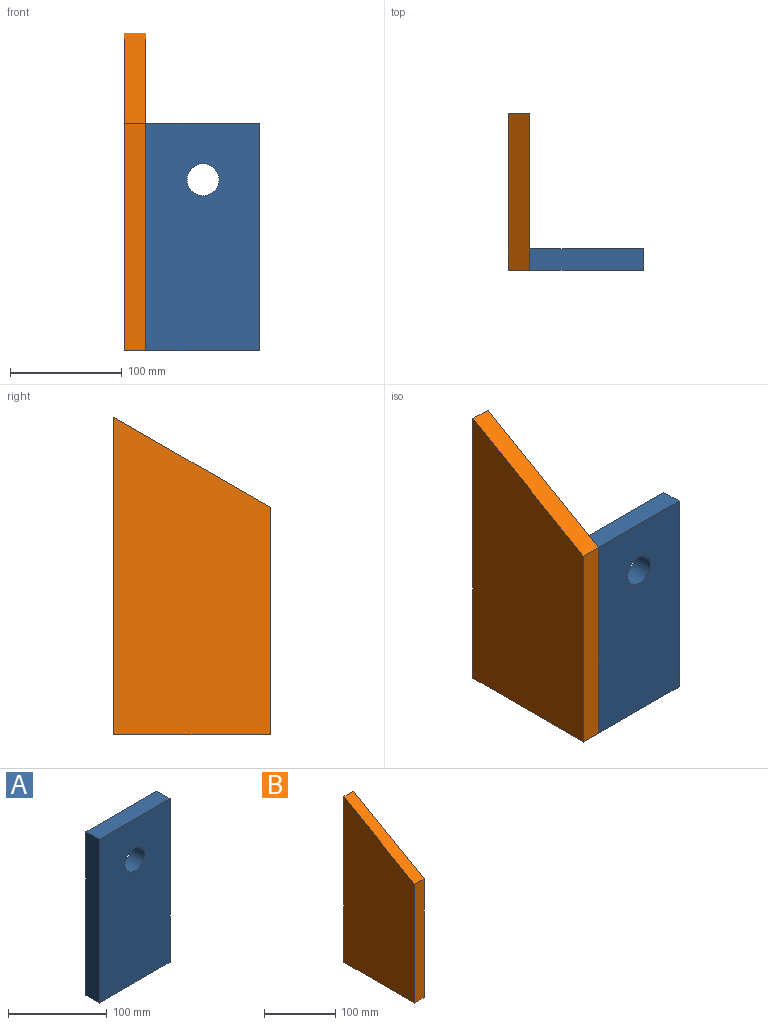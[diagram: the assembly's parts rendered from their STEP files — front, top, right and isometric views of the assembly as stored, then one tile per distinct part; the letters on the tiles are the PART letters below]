
ASSEMBLY  parts=2 mates=1
PART A: 7 faces, bbox 101.6x19.1x203.2 mm
  f0: plane 203.2x19.05mm, normal (-1,0,0), area 3871mm2, adj f1,f3,f5,f6
  f1: plane 101.6x19.05mm, normal (0,0,-1), area 1935.5mm2, adj f0,f2,f5,f6
  f2: plane 203.2x19.05mm, normal (1,0,0), area 3871mm2, adj f1,f3,f5,f6
  f3: plane 101.6x19.05mm, normal (0,0,1), area 1935.5mm2, adj f0,f2,f5,f6
  f4: cylinder r=14.29mm len=28.58mm, axis (0,1,0), area 1710.1mm2, adj f5,f6
  f5: plane 203.2x101.6mm, normal (0,-1,0), area 20003.8mm2, adj f0,f1,f2,f3,f4
  f6: plane 203.2x101.6mm, normal (0,1,0), area 20003.8mm2, adj f0,f1,f2,f3,f4
PART B: 6 faces, bbox 19.1x139.7x283.9 mm
  f0: plane 283.86x19.05mm, normal (0,1,0), area 5407.5mm2, adj f1,f3,f4,f5
  f1: plane 283.86x139.7mm, normal (-1,0,0), area 34020.8mm2, adj f0,f2,f4,f5
  f2: plane 203.2x19.05mm, normal (0,-1,0), area 3871mm2, adj f1,f3,f4,f5
  f3: plane 283.86x139.7mm, normal (1,0,0), area 34020.8mm2, adj f0,f2,f4,f5
  f4: plane 139.7x80.66mm, normal (0,-0.5,0.87), area 3073mm2, adj f0,f1,f2,f3
  f5: plane 139.7x19.05mm, normal (0,0,-1), area 2661.3mm2, adj f0,f1,f2,f3
PLACE A t=(-159.51,35.05,23.98)mm
PLACE B t=(-156.57,93.17,6.17)mm
MATE fastened B.f5 <-> A.f1  axis (0,0,-1) through (-186.4,16,6.17)mm
